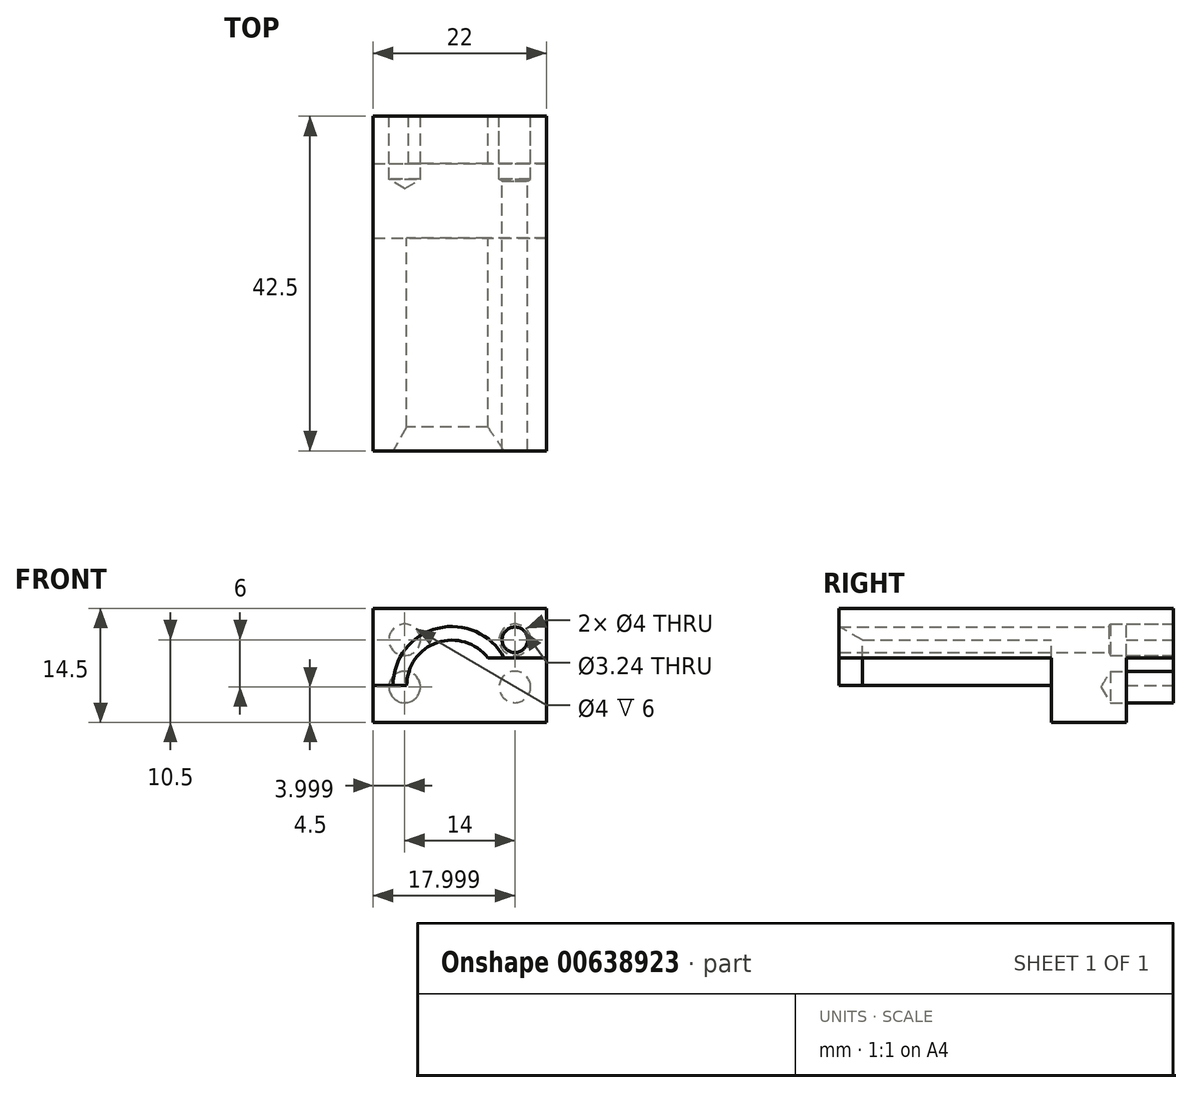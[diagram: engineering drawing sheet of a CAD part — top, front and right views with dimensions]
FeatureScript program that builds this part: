
annotation { "Feature Type Name" : "Feature", "Feature Type Description" : "" }
export const myFeature = defineFeature(function(context is Context, id is Id, definition is map)
    precondition{}
    {
        {
            var Q0;
            Q0=qCreatedBy(makeId("Front.planeOp"),FACE);
            var sketch = newSketch(context, id + "F0", { "sketchPlane" : qUnion([Q0])});
            skArc(sketch, "E0", {"start": v(-79.87, 0.95) * mm, "mid": v(-88.3, 4.73) * mm, "end": v(-94, -2.55) * mm});
            skArc(sketch, "E1", {"start": v(-81.94, 0.95) * mm, "mid": v(-88.35, 2.9) * mm, "end": v(-92.25, -2.55) * mm});
            skLineSegment(sketch, "E2", {"start": v(-74.5, 0.95) * mm, "end": v(-81.94, 0.95) * mm});
            skLineSegment(sketch, "E3", {"start": v(-96.5, 7.25) * mm, "end": v(-74.5, 7.25) * mm});
            skLineSegment(sketch, "E4", {"start": v(-74.5, -7.25) * mm, "end": v(-74.5, 7.25) * mm});
            skCircle(sketch, "E5", {"center": v(-78.5, 3.25) * mm, "radius": 1.62 * mm});
            skArc(sketch, "E6", {"start": v(-79.02, 1.32) * mm, "mid": v(-76.77, 4.25) * mm, "end": v(-80.43, 3.77) * mm});
            skCircle(sketch, "E7", {"center": v(-92.5, 3.25) * mm, "radius": 2 * mm});
            skArc(sketch, "E8", {"start": v(-90.57, -2.23) * mm, "mid": v(-94.23, -1.75) * mm, "end": v(-91.98, -4.68) * mm});
            skCircle(sketch, "E9", {"center": v(-92.5, -2.75) * mm, "radius": 1.62 * mm});
            skCircle(sketch, "E10", {"center": v(-78.5, -2.75) * mm, "radius": 2 * mm});
            skLineSegment(sketch, "E11", {"start": v(-96.5, -2.55) * mm, "end": v(-92.16, -2.55) * mm});
            skLineSegment(sketch, "E12", {"start": v(-96.5, -7.25) * mm, "end": v(-74.5, -7.25) * mm});
            skLineSegment(sketch, "E13", {"start": v(-96.5, -7.25) * mm, "end": v(-96.5, 7.25) * mm});
            skLineSegment(sketch, "E14", {"start": v(57.03, 3.2) * mm, "end": v(57.03, -2.55) * mm});
            skLineSegment(sketch, "E15", {"start": v(57.03, 3.2) * mm, "end": v(81, 3.2) * mm});
            skLineSegment(sketch, "E16", {"start": v(57.03, 3.2) * mm, "end": v(54, 4.95) * mm});
            skLineSegment(sketch, "E17", {"start": v(81, -7.25) * mm, "end": v(81, 3.2) * mm});
            skLineSegment(sketch, "E18", {"start": v(54, 7.25) * mm, "end": v(54, -7.25) * mm});
            skLineSegment(sketch, "E19", {"start": v(81, -2.55) * mm, "end": v(54, -2.55) * mm});
            skLineSegment(sketch, "E20", {"start": v(54, -7.25) * mm, "end": v(96.5, -7.25) * mm});
            skLineSegment(sketch, "E21", {"start": v(54, 7.25) * mm, "end": v(96.5, 7.25) * mm});
            skLineSegment(sketch, "E22", {"start": v(96.5, -7.25) * mm, "end": v(96.5, 7.25) * mm});
            skSolve(sketch);
        }
        {
            var Q0;
            {var subQ0=sQuery(id+"F0.wireOp",EDGE,"E2");var subQ1=sQuery(id+"F0.wireOp",EDGE,"E0");var subQ2=makeQuery(id+"F0.imprint","INTERSECT",VERTEX,{"derivedFrom":[subQ1,subQ0]});Q0=makeQuery(id+"F0.imprint","IMPRINT",FACE,{"disambiguationData":[TD([[makeQuery(id+"F0.imprint","IMPRINT",EDGE,{"disambiguationData":[TD([[subQ2,-1.0]])],"derivedFrom":subQ1}),1.0]])]});}
            var Q1;
            {var subQ9=sQuery(id+"F0.wireOp",EDGE,"E3");Q1=makeQuery(id+"F0.imprint","IMPRINT",FACE,{"disambiguationData":[TD([[makeQuery(id+"F0.imprint","IMPRINT",EDGE,{"derivedFrom":subQ9}),-1.0]])]});}
            var Q2;
            Q2=makeQuery(id+"F0.imprint","IMPRINT",FACE,{"disambiguationData":[TD([[makeQuery(id+"F0.imprint","IMPRINT",EDGE,{"derivedFrom":sQuery(id+"F0.wireOp",EDGE,"E10")}),1.0]])]});
            var Q3;
            {var subQ0=sQuery(id+"F0.wireOp",EDGE,"E7");var subQ1=sQuery(id+"F0.wireOp",EDGE,"E0");var subQ2=makeQuery(id+"F0.imprint","INTERSECT",VERTEX,{"disambiguationData":[OD(0.0)],"derivedFrom":[subQ1,subQ0]});Q3=makeQuery(id+"F0.imprint","IMPRINT",FACE,{"disambiguationData":[TD([[makeQuery(id+"F0.imprint","IMPRINT",EDGE,{"disambiguationData":[TD([[subQ2,-1.0]])],"derivedFrom":subQ1}),-1.0]])]});}
            var Q4;
            Q4=makeQuery(id+"F0.imprint","IMPRINT",FACE,{"disambiguationData":[TD([[makeQuery(id+"F0.imprint","IMPRINT",EDGE,{"derivedFrom":sQuery(id+"F0.wireOp",EDGE,"E10")}),-1.0]])]});
            var Q5;
            {var subQ0=sQuery(id+"F0.wireOp",EDGE,"E7");var subQ1=sQuery(id+"F0.wireOp",EDGE,"E0");var subQ2=makeQuery(id+"F0.imprint","INTERSECT",VERTEX,{"disambiguationData":[OD(0.0)],"derivedFrom":[subQ1,subQ0]});Q5=makeQuery(id+"F0.imprint","IMPRINT",FACE,{"disambiguationData":[TD([[makeQuery(id+"F0.imprint","IMPRINT",EDGE,{"disambiguationData":[TD([[subQ2,-1.0]])],"derivedFrom":subQ1}),1.0]])]});}
            var Q6;
            Q6=makeQuery(id+"F0.imprint","IMPRINT",FACE,{"disambiguationData":[TD([[makeQuery(id+"F0.imprint","IMPRINT",EDGE,{"derivedFrom":sQuery(id+"F0.wireOp",EDGE,"E5")}),-1.0]])]});
            var Q7;
            {var subQ0=sQuery(id+"F0.wireOp",EDGE,"E8");var subQ1=sQuery(id+"F0.wireOp",EDGE,"E0");var subQ2=makeQuery(id+"F0.imprint","INTERSECT",VERTEX,{"derivedFrom":[subQ1,subQ0]});Q7=makeQuery(id+"F0.imprint","IMPRINT",FACE,{"disambiguationData":[TD([[makeQuery(id+"F0.imprint","IMPRINT",EDGE,{"disambiguationData":[TD([[subQ2,-1.0]])],"derivedFrom":subQ1}),-1.0]])]});}
            var Q8;
            {var subQ0=sQuery(id+"F0.wireOp",EDGE,"E8");var subQ1=sQuery(id+"F0.wireOp",EDGE,"E0");var subQ2=makeQuery(id+"F0.imprint","INTERSECT",VERTEX,{"derivedFrom":[subQ1,subQ0]});Q8=makeQuery(id+"F0.imprint","IMPRINT",FACE,{"disambiguationData":[TD([[makeQuery(id+"F0.imprint","IMPRINT",EDGE,{"disambiguationData":[TD([[subQ2,-1.0]])],"derivedFrom":subQ1}),1.0]])]});}
            var Q9;
            {var subQ0=sQuery(id+"F0.wireOp",EDGE,"E11");var subQ1=sQuery(id+"F0.wireOp",EDGE,"E1");var subQ2=makeQuery(id+"F0.imprint","INTERSECT",VERTEX,{"derivedFrom":[subQ1,subQ0]});Q9=makeQuery(id+"F0.imprint","IMPRINT",FACE,{"disambiguationData":[TD([[makeQuery(id+"F0.imprint","IMPRINT",EDGE,{"disambiguationData":[TD([[subQ2,1.0]])],"derivedFrom":subQ1}),1.0]])]});}
            var Q10;
            {var subQ0=sQuery(id+"F0.wireOp",EDGE,"E11");var subQ1=sQuery(id+"F0.wireOp",EDGE,"E0");var subQ2=makeQuery(id+"F0.imprint","INTERSECT",VERTEX,{"derivedFrom":[subQ1,subQ0]});Q10=makeQuery(id+"F0.imprint","IMPRINT",FACE,{"disambiguationData":[TD([[makeQuery(id+"F0.imprint","IMPRINT",EDGE,{"disambiguationData":[TD([[subQ2,1.0]])],"derivedFrom":subQ1}),1.0]])]});}
            var Q11;
            {var subQ0=sQuery(id+"F0.wireOp",EDGE,"E11");var subQ1=sQuery(id+"F0.wireOp",EDGE,"E0");var subQ2=makeQuery(id+"F0.imprint","INTERSECT",VERTEX,{"derivedFrom":[subQ1,subQ0]});Q11=makeQuery(id+"F0.imprint","IMPRINT",FACE,{"disambiguationData":[TD([[makeQuery(id+"F0.imprint","IMPRINT",EDGE,{"disambiguationData":[TD([[subQ2,1.0]])],"derivedFrom":subQ1}),-1.0]])]});}
            extrude(context, id + "F1", {"entities" : qUnion([Q0, Q1, Q2, Q3, Q4, Q5, Q6, Q7, Q8, Q9, Q10, Q11]), "depth" : 15.5 * mm, "offsetDistance" : 25 * mm});
        }
        {
            var Q0;
            Q0=makeQuery(id+"F1.opExtrude","CAP_FACE",FACE,{"disambiguationData":[OSD([sQuery(id+"F0.wireOp",EDGE,"E3"),sQuery(id+"F0.wireOp",EDGE,"E4"),sQuery(id+"F0.wireOp",EDGE,"E12"),sQuery(id+"F0.wireOp",EDGE,"E13")])],"isStart":false});
            var sketch = newSketch(context, id + "F2", { "sketchPlane" : qUnion([Q0])});
            skLineSegment(sketch, "E23.0", {"start": v(-74.5, 0.95) * mm, "end": v(-81.94, 0.95) * mm});
            skArc(sketch, "E24.0", {"start": v(-81.94, 0.95) * mm, "mid": v(-88.35, 2.9) * mm, "end": v(-92.25, -2.55) * mm});
            skLineSegment(sketch, "E25.0", {"start": v(-96.5, -2.55) * mm, "end": v(-92.16, -2.55) * mm});
            skLineSegment(sketch, "E26.0", {"start": v(-96.5, -7.25) * mm, "end": v(-96.5, 7.25) * mm});
            skLineSegment(sketch, "E27.0", {"start": v(-96.5, 7.25) * mm, "end": v(-74.5, 7.25) * mm});
            skLineSegment(sketch, "E28.0", {"start": v(-74.5, -7.25) * mm, "end": v(-74.5, 7.25) * mm});
            skSolve(sketch);
        }
        {
            var Q0;
            {var subQ5=sQuery(id+"F2.wireOp",EDGE,"E23.0");Q0=makeQuery(id+"F2.imprint","IMPRINT",FACE,{"disambiguationData":[TD([[makeQuery(id+"F2.imprint","IMPRINT",EDGE,{"derivedFrom":subQ5}),-1.0]])]});}
            extrude(context, id + "F3", {"entities" : qUnion([Q0]), "operationType" : NewBodyOperationType.ADD, "depth" : 27 * mm, "offsetDistance" : 25 * mm});
        }
        {
            var Q0;
            Q0=sQuery(id+"F0.wireOp",VERTEX,"E8.center");
            var Q1;
            Q1=sQuery(id+"F0.wireOp",VERTEX,"E5.center");
            var Q2;
            Q2=makeQuery(id+"F1.opExtrude","SWEPT_BODY",BODY,{"disambiguationData":[OSD([sQuery(id+"F0.wireOp",EDGE,"E3"),sQuery(id+"F0.wireOp",EDGE,"E4"),sQuery(id+"F0.wireOp",EDGE,"E12"),sQuery(id+"F0.wireOp",EDGE,"E13")])]});
            hole(context, id + "F4", {"style" : HoleStyle.SIMPLE, "endStyle" : HoleEndStyle.BLIND, "oppositeDirection" : true, "holeDiameter" : 4 * mm, "majorDiameter" : 5 * mm, "holeDepth" : 8 * mm, "isTappedThrough" : true, "tappedDepth" : 12 * mm, "tapClearance" : 3, "locations" : qUnion([Q0, Q1]), "scope" : qUnion([Q2])});
        }
        {
            var Q0;
            {var subQ0=sQuery(id+"F0.wireOp",EDGE,"E7");var subQ1=sQuery(id+"F0.wireOp",EDGE,"E0");var subQ2=makeQuery(id+"F0.imprint","INTERSECT",VERTEX,{"disambiguationData":[OD(0.0)],"derivedFrom":[subQ1,subQ0]});Q0=makeQuery(id+"F0.imprint","IMPRINT",FACE,{"disambiguationData":[TD([[makeQuery(id+"F0.imprint","IMPRINT",EDGE,{"disambiguationData":[TD([[subQ2,-1.0]])],"derivedFrom":subQ1}),-1.0]])]});}
            var Q1;
            {var subQ0=sQuery(id+"F0.wireOp",EDGE,"E7");var subQ1=sQuery(id+"F0.wireOp",EDGE,"E0");var subQ2=makeQuery(id+"F0.imprint","INTERSECT",VERTEX,{"disambiguationData":[OD(0.0)],"derivedFrom":[subQ1,subQ0]});Q1=makeQuery(id+"F0.imprint","IMPRINT",FACE,{"disambiguationData":[TD([[makeQuery(id+"F0.imprint","IMPRINT",EDGE,{"disambiguationData":[TD([[subQ2,-1.0]])],"derivedFrom":subQ1}),1.0]])]});}
            var Q2;
            Q2=makeQuery(id+"F0.imprint","IMPRINT",FACE,{"disambiguationData":[TD([[makeQuery(id+"F0.imprint","IMPRINT",EDGE,{"derivedFrom":sQuery(id+"F0.wireOp",EDGE,"E10")}),-1.0]])]});
            extrude(context, id + "F5", {"entities" : qUnion([Q0, Q1, Q2]), "operationType" : NewBodyOperationType.REMOVE, "depth" : 6 * mm, "offsetDistance" : 25 * mm});
        }
        {
            var Q0;
            Q0=makeQuery(id+"F3.opExtrude","CAP_EDGE",EDGE,{"disambiguationData":[OSD([sQuery(id+"F2.wireOp",EDGE,"E24.0")])],"isStart":false});
            chamfer(context, id + "F6", {"entities" : qUnion([Q0]), "chamferType" : ChamferType.OFFSET_ANGLE, "width" : 3 * mm, "oppositeDirection" : false, "angle" : 30 * degree, "tangentPropagation" : true});
        }
    });
